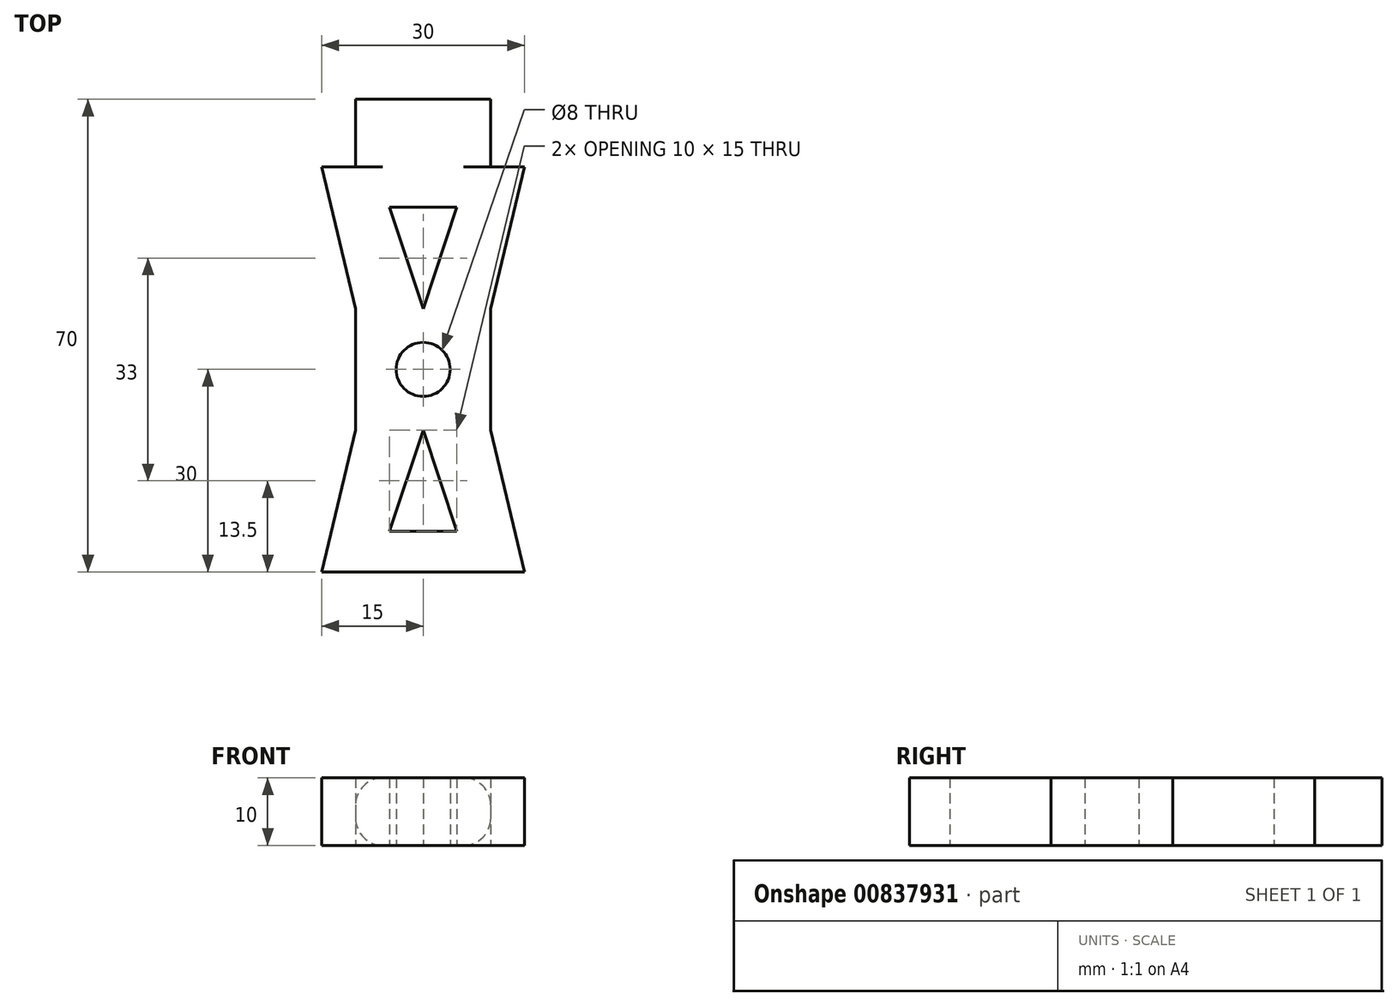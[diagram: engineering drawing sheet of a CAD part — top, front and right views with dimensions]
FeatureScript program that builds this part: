
annotation { "Feature Type Name" : "Feature", "Feature Type Description" : "" }
export const myFeature = defineFeature(function(context is Context, id is Id, definition is map)
    precondition{}
    {
        {
            var Q0;
            Q0=qCreatedBy(makeId("Top.planeOp"),FACE);
            var sketch = newSketch(context, id + "F0", { "sketchPlane" : qUnion([Q0])});
            skLineSegment(sketch, "E0.bottom", {"start": v(25, 30) * mm, "end": v(-25, 30) * mm});
            skLineSegment(sketch, "E0.top", {"start": v(25, -30) * mm, "end": v(-25, -30) * mm});
            skLineSegment(sketch, "E0.left", {"start": v(25, 30) * mm, "end": v(25, -30) * mm});
            skLineSegment(sketch, "E0.right", {"start": v(-25, 30) * mm, "end": v(-25, -30) * mm});
            skPoint(sketch, "E0.middle", {"position": v(0, 0) * mm});
            skCircle(sketch, "E1", {"center": v(0, 0) * mm, "radius": 4 * mm});
            skLineSegment(sketch, "E2.bottom", {"start": v(-10, 30) * mm, "end": v(10, 30) * mm});
            skLineSegment(sketch, "E2.top", {"start": v(-10, 40) * mm, "end": v(10, 40) * mm});
            skLineSegment(sketch, "E2.left", {"start": v(-10, 30) * mm, "end": v(-10, 40) * mm});
            skLineSegment(sketch, "E2.right", {"start": v(10, 30) * mm, "end": v(10, 40) * mm});
            skLineSegment(sketch, "E3.bottom", {"start": v(-10, -30) * mm, "end": v(10, -30) * mm});
            skLineSegment(sketch, "E3.top", {"start": v(-10, -40) * mm, "end": v(10, -40) * mm});
            skLineSegment(sketch, "E3.left", {"start": v(-10, -30) * mm, "end": v(-10, -40) * mm});
            skLineSegment(sketch, "E3.right", {"start": v(10, -30) * mm, "end": v(10, -40) * mm});
            skLineSegment(sketch, "E4", {"start": v(0, -9) * mm, "end": v(-5, -24) * mm});
            skLineSegment(sketch, "E5", {"start": v(-5, -24) * mm, "end": v(5, -24) * mm});
            skLineSegment(sketch, "E6", {"start": v(5, -24) * mm, "end": v(0, -9) * mm});
            skLineSegment(sketch, "E7", {"start": v(-15, -30) * mm, "end": v(-10, -9) * mm});
            skLineSegment(sketch, "E8", {"start": v(-10, -9) * mm, "end": v(-10, 0) * mm});
            skPoint(sketch, "E8.endSnap0", {"position": v(-25, 0) * mm});
            skLineSegment(sketch, "E9", {"start": v(-10, 0) * mm, "end": v(-25, 0) * mm});
            skLineSegment(sketch, "E10.MirrorCS", {"start": v(15, -30) * mm, "end": v(10, -9) * mm});
            skLineSegment(sketch, "E11.MirrorCS", {"start": v(10, -9) * mm, "end": v(10, 0) * mm});
            skLineSegment(sketch, "E12.MirrorCS", {"start": v(10, 0) * mm, "end": v(25, 0) * mm});
            skPoint(sketch, "E13.MirrorP", {"position": v(25, 0) * mm});
            skLineSegment(sketch, "E14.MirrorCS", {"start": v(0, 9) * mm, "end": v(-5, 24) * mm});
            skLineSegment(sketch, "E15.MirrorCS", {"start": v(5, 24) * mm, "end": v(0, 9) * mm});
            skLineSegment(sketch, "E16.MirrorCS", {"start": v(-5, 24) * mm, "end": v(5, 24) * mm});
            skLineSegment(sketch, "E17.MirrorCS", {"start": v(10, 9) * mm, "end": v(10, 0) * mm});
            skLineSegment(sketch, "E18.MirrorCS", {"start": v(15, 30) * mm, "end": v(10, 9) * mm});
            skLineSegment(sketch, "E19.MirrorCS", {"start": v(-10, 9) * mm, "end": v(-10, 0) * mm});
            skLineSegment(sketch, "E20.MirrorCS", {"start": v(-15, 30) * mm, "end": v(-10, 9) * mm});
            skSolve(sketch);
        }
        {
            var Q0;
            Q0=makeQuery(id+"F0.imprint","IMPRINT",FACE,{"disambiguationData":[TD([[makeQuery(id+"F0.imprint","IMPRINT",EDGE,{"derivedFrom":sQuery(id+"F0.wireOp",EDGE,"E1")}),-1.0]])]});
            var Q1;
            Q1=makeQuery(id+"F0.imprint","IMPRINT",FACE,{"disambiguationData":[TD([[makeQuery(id+"F0.imprint","IMPRINT",EDGE,{"derivedFrom":sQuery(id+"F0.wireOp",EDGE,"E2.top")}),-1.0]])]});
            var Q2;
            Q2=makeQuery(id+"F0.imprint","IMPRINT",FACE,{"disambiguationData":[TD([[makeQuery(id+"F0.imprint","IMPRINT",EDGE,{"derivedFrom":sQuery(id+"F0.wireOp",EDGE,"E3.bottom")}),-1.0]])]});
            extrude(context, id + "F1", {"entities" : qUnion([Q0, Q1, Q2]), "depth" : 10 * mm, "offsetDistance" : 25 * mm});
        }
        {
            var Q0;
            Q0=makeQuery(id+"F1.opExtrude","CAP_EDGE",EDGE,{"disambiguationData":[OSD([sQuery(id+"F0.wireOp",EDGE,"E3.left")])],"isStart":false});
            var Q1;
            Q1=makeQuery(id+"F1.opExtrude","CAP_EDGE",EDGE,{"disambiguationData":[OSD([sQuery(id+"F0.wireOp",EDGE,"E3.right")])],"isStart":false});
            var Q2;
            Q2=makeQuery(id+"F1.opExtrude","CAP_EDGE",EDGE,{"disambiguationData":[OSD([sQuery(id+"F0.wireOp",EDGE,"E3.left")])],"isStart":true});
            var Q3;
            Q3=makeQuery(id+"F1.opExtrude","CAP_EDGE",EDGE,{"disambiguationData":[OSD([sQuery(id+"F0.wireOp",EDGE,"E3.right")])],"isStart":true});
            var Q4;
            Q4=makeQuery(id+"F1.opExtrude","CAP_EDGE",EDGE,{"disambiguationData":[OSD([sQuery(id+"F0.wireOp",EDGE,"E2.right")])],"isStart":true});
            var Q5;
            Q5=makeQuery(id+"F1.opExtrude","CAP_EDGE",EDGE,{"disambiguationData":[OSD([sQuery(id+"F0.wireOp",EDGE,"E2.left")])],"isStart":true});
            var Q6;
            Q6=makeQuery(id+"F1.opExtrude","CAP_EDGE",EDGE,{"disambiguationData":[OSD([sQuery(id+"F0.wireOp",EDGE,"E2.left")])],"isStart":false});
            var Q7;
            Q7=makeQuery(id+"F1.opExtrude","CAP_EDGE",EDGE,{"disambiguationData":[OSD([sQuery(id+"F0.wireOp",EDGE,"E2.right")])],"isStart":false});
            fillet(context, id + "F2", {"entities" : qUnion([Q0, Q1, Q2, Q3, Q4, Q5, Q6, Q7]), "radius" : 4 * mm, "tangentPropagation" : true, "allowEdgeOverflow" : false});
        }
    });
